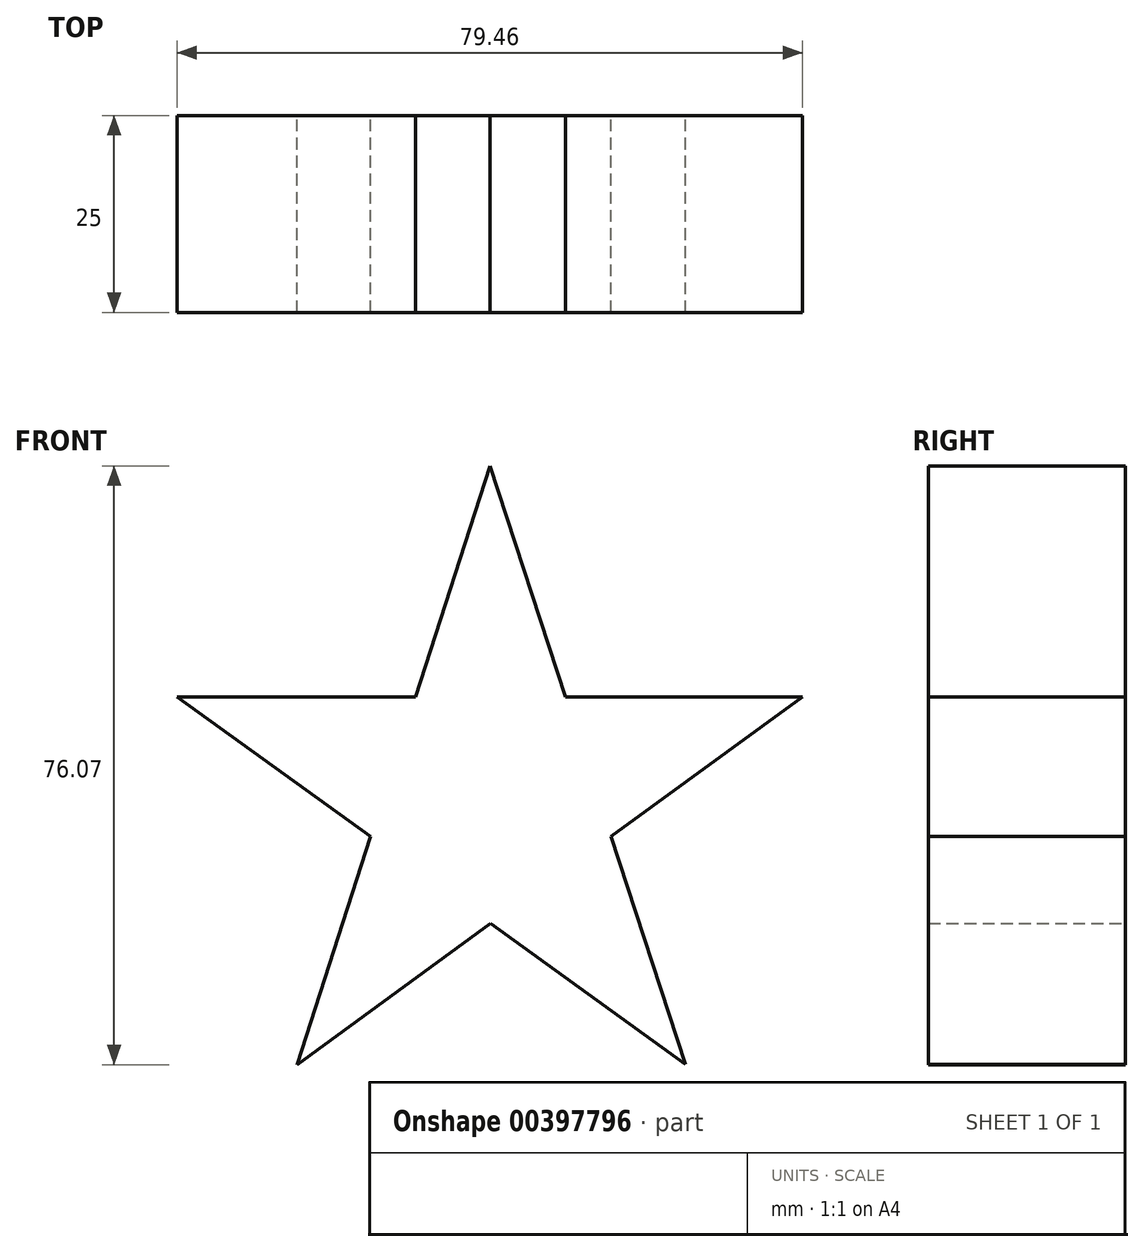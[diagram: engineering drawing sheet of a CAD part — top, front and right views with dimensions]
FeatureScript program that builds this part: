
annotation { "Feature Type Name" : "Feature", "Feature Type Description" : "" }
export const myFeature = defineFeature(function(context is Context, id is Id, definition is map)
    precondition{}
    {
        {
            var Q0;
            Q0=qCreatedBy(makeId("Front.planeOp"),FACE);
            var sketch = newSketch(context, id + "F0", { "sketchPlane" : qUnion([Q0])});
            skCircle(sketch, "E0.cCircle", {"center": v(0, 0) * mm, "radius": 33.8 * mm, "construction": true});
            skLineSegment(sketch, "E0.0", {"start": v(-39.74, 12.88) * mm, "end": v(-0.03, 41.77) * mm});
            skLineSegment(sketch, "E0.1", {"start": v(-0.03, 41.77) * mm, "end": v(39.72, 12.93) * mm});
            skLineSegment(sketch, "E0.2", {"start": v(39.72, 12.93) * mm, "end": v(24.58, -33.78) * mm});
            skLineSegment(sketch, "E0.3", {"start": v(24.58, -33.78) * mm, "end": v(-24.53, -33.81) * mm});
            skLineSegment(sketch, "E0.4", {"start": v(-24.53, -33.81) * mm, "end": v(-39.74, 12.88) * mm});
            skPoint(sketch, "E0.0.midPoint", {"position": v(-19.88, 27.33) * mm});
            skSolve(sketch);
        }
        {
            var Q0;
            Q0=makeQuery(id+"F0.imprint","IMPRINT",FACE,{"disambiguationData":[TD([[makeQuery(id+"F0.imprint","IMPRINT",EDGE,{"derivedFrom":sQuery(id+"F0.wireOp",EDGE,"E0.0")}),-1.0]])]});
            var sketch = newSketch(context, id + "F1", { "sketchPlane" : qUnion([Q0])});
            skLineSegment(sketch, "E1", {"start": v(0, 42.28) * mm, "end": v(-24.51, -33.79) * mm});
            skLineSegment(sketch, "E2", {"start": v(-24.51, -33.79) * mm, "end": v(39.72, 12.93) * mm});
            skLineSegment(sketch, "E3", {"start": v(39.72, 12.93) * mm, "end": v(-39.74, 12.93) * mm});
            skLineSegment(sketch, "E4", {"start": v(-39.74, 12.93) * mm, "end": v(24.86, -33.75) * mm});
            skLineSegment(sketch, "E5", {"start": v(24.86, -33.75) * mm, "end": v(0, 42.28) * mm});
            skSolve(sketch);
        }
        {
            var Q0;
            Q0 = qSketchRegion(id + "F1", true);
            extrude(context, id + "F2", {"entities" : qUnion([Q0]), "depth" : 25 * mm});
        }
    });
